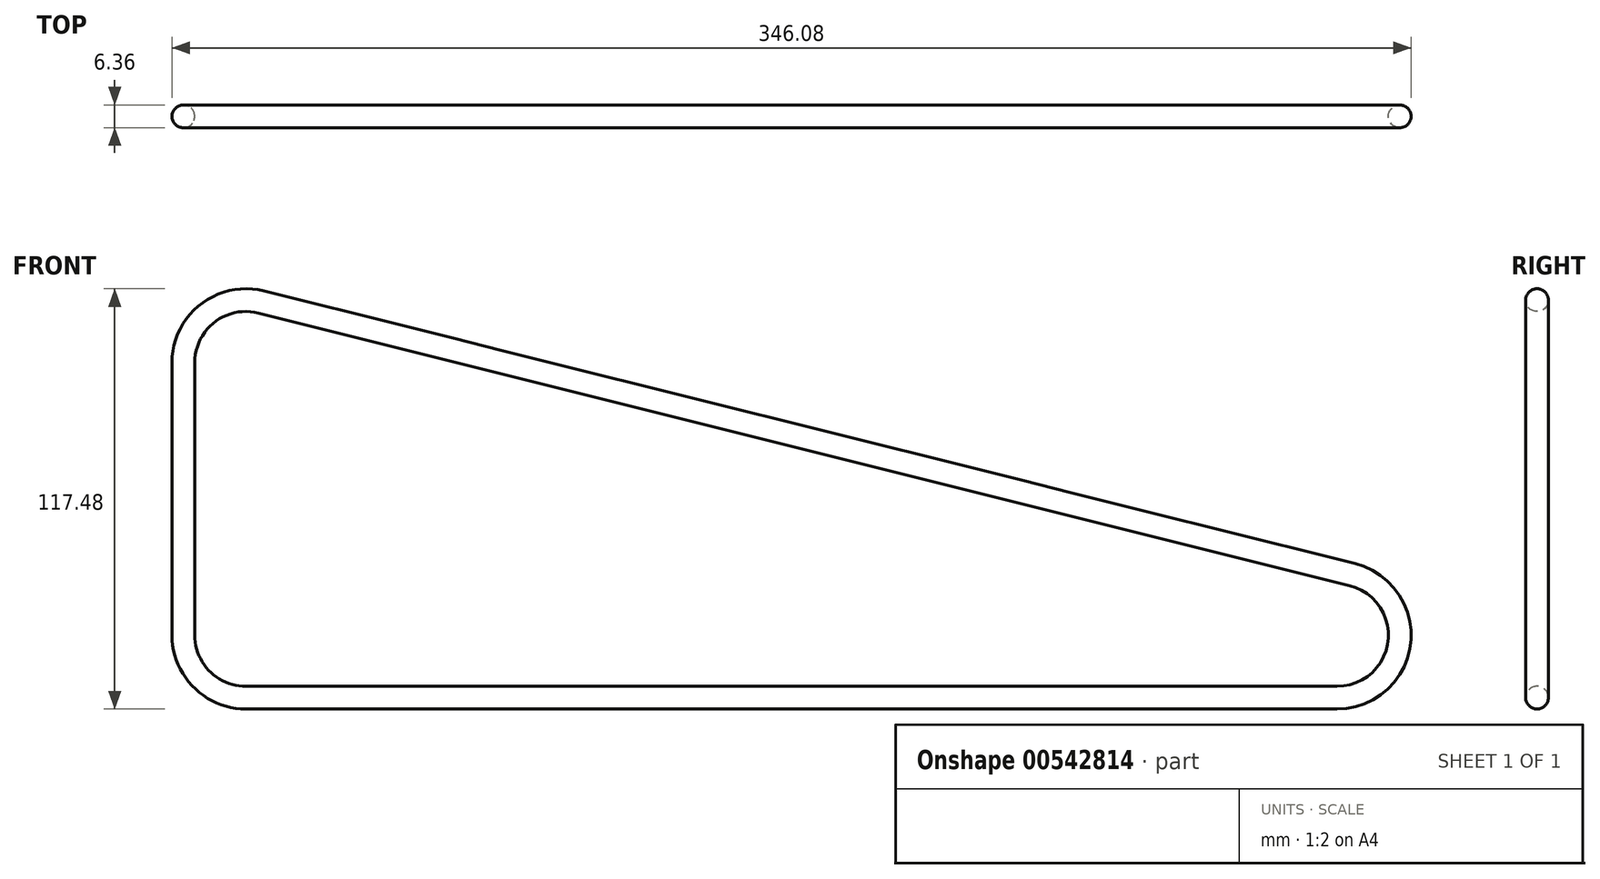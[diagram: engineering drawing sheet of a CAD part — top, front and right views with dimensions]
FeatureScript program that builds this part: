
annotation { "Feature Type Name" : "Feature", "Feature Type Description" : "" }
export const myFeature = defineFeature(function(context is Context, id is Id, definition is map)
    precondition{}
    {
        {
            var Q0;
            Q0=qCreatedBy(makeId("Front.planeOp"),FACE);
            var sketch = newSketch(context, id + "F0", { "sketchPlane" : qUnion([Q0])});
            skArc(sketch, "E0", {"start": v(-300.56, 110.6) * mm, "mid": v(-315.55, 107.43) * mm, "end": v(-322.26, 93.66) * mm});
            skArc(sketch, "E1", {"start": v(-322.26, 17.46) * mm, "mid": v(-317.15, 5.11) * mm, "end": v(-304.8, 0) * mm});
            skArc(sketch, "E2", {"start": v(0, 0) * mm, "mid": v(17.33, 15.33) * mm, "end": v(4.24, 34.4) * mm});
            skLineSegment(sketch, "E3", {"start": v(-304.8, 0) * mm, "end": v(0, 0) * mm});
            skLineSegment(sketch, "E4", {"start": v(-322.26, 17.46) * mm, "end": v(-322.26, 93.66) * mm});
            skLineSegment(sketch, "E5", {"start": v(-300.56, 110.6) * mm, "end": v(4.24, 34.4) * mm});
            skSolve(sketch);
        }
        {
            var Q0;
            Q0=qCreatedBy(makeId("Right.planeOp"),FACE);
            var sketch = newSketch(context, id + "F1", { "sketchPlane" : qUnion([Q0])});
            skCircle(sketch, "E6", {"center": v(0, 0) * mm, "radius": 3.18 * mm});
            skSolve(sketch);
        }
        {
            var Q0;
            Q0=makeQuery(id+"F1.imprint","IMPRINT",FACE,{"disambiguationData":[TD([[makeQuery(id+"F1.imprint","IMPRINT",EDGE,{"derivedFrom":sQuery(id+"F1.wireOp",EDGE,"E6")}),1.0]])]});
            var Q1;
            Q1=sQuery(id+"F0.wireOp",EDGE,"E3");
            var Q2;
            Q2=sQuery(id+"F0.wireOp",EDGE,"E1");
            var Q3;
            Q3=sQuery(id+"F0.wireOp",EDGE,"E4");
            var Q4;
            Q4=sQuery(id+"F0.wireOp",EDGE,"E0");
            var Q5;
            Q5=sQuery(id+"F0.wireOp",EDGE,"E5");
            var Q6;
            Q6=sQuery(id+"F0.wireOp",EDGE,"E2");
            sweep(context, id + "F2", {"profiles" : qUnion([Q0]), "path" : qUnion([Q1, Q2, Q3, Q4, Q5, Q6])});
        }
    });
